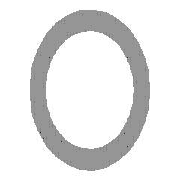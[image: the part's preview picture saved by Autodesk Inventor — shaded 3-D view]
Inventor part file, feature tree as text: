
AUTODESK INVENTOR PART (.ipt)
format: ipt  version: 2021 (Build 250183000, 183)  size: 121,856 bytes
history: native  units: mm (DEFAULTED — no unit token found)
features: other x5, plane x2, sketch x2, sweep x1
ambient origin geometry x8: Origin, YZ Plane, XZ Plane, XY Plane, X Axis, Y Axis, Z Axis, Center Point
bodies: Solid1 (feature_tree)
feature tree (10):
  parser-record x1  (decoder bookkeeping rows leaked as tree rows — omitted from the tree; the rows remain in map.json)
  other  "Driven Length"
  other  "Plano inicial"
  other  "Plano final"
  other  "Trayectoria de barrido"
  plane  "Plano de trabajo de orientación"
  sweep  "Cuerpo"
  sketch  "Sketch3"  dims[d0=60.452mm d1=5.5372mm]
  plane  "Work Plane3"
  sketch  "Sketch4"  dims[d4=-0.0mm d5=72.0mm d6=90.0deg d7=72.0mm d8=0.0mm d9=0.0mm]
